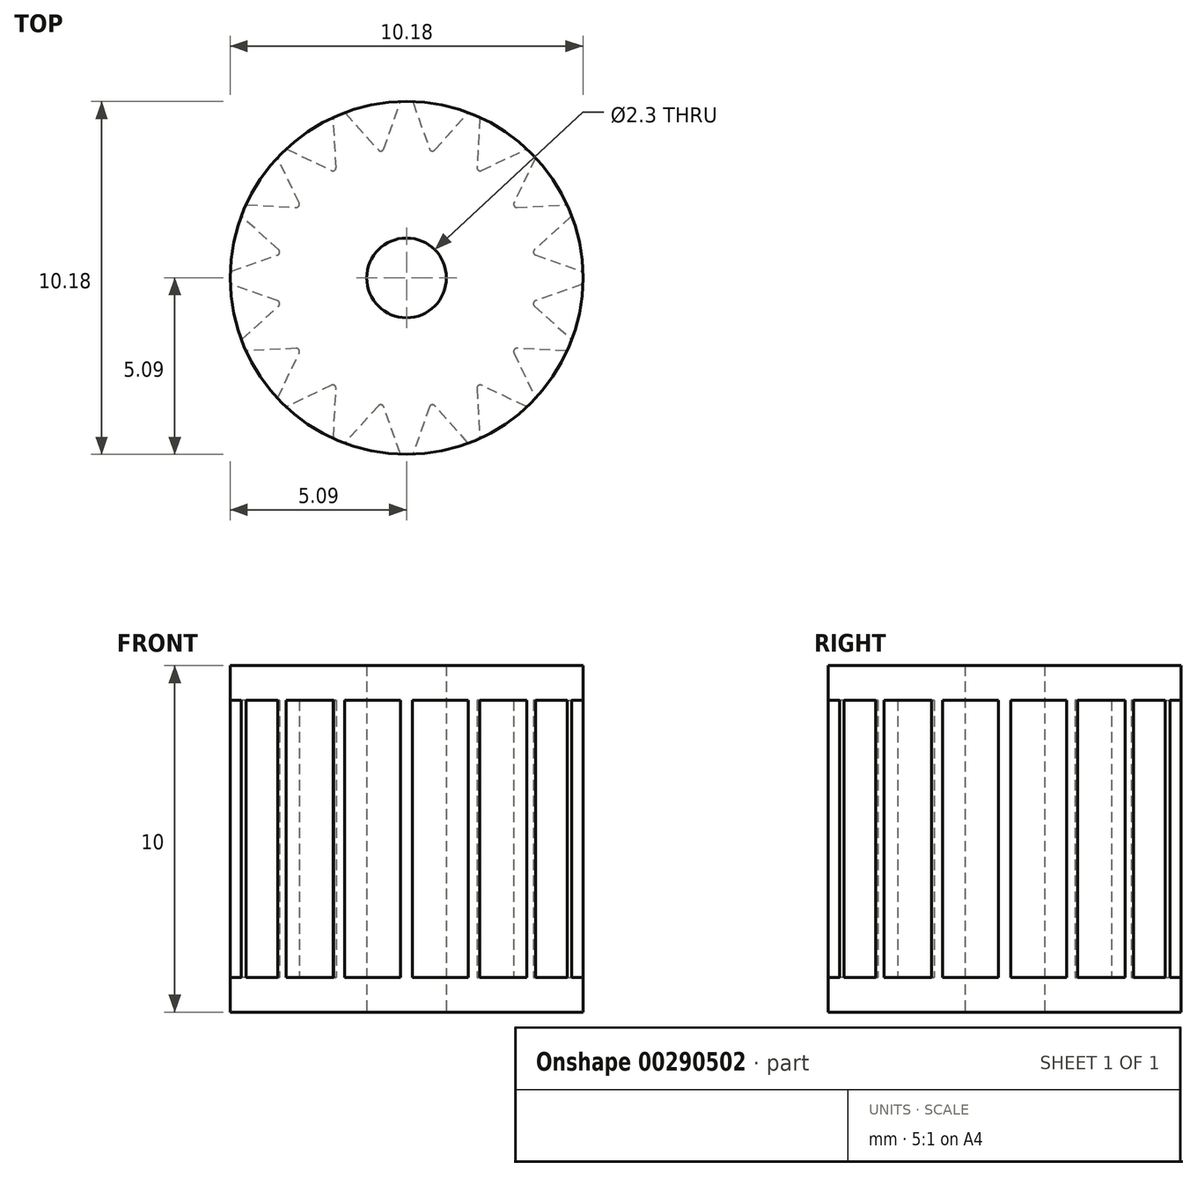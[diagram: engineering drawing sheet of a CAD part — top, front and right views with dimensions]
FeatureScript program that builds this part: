
annotation { "Feature Type Name" : "Feature", "Feature Type Description" : "" }
export const myFeature = defineFeature(function(context is Context, id is Id, definition is map)
    precondition{}
    {
        {
            var Q0;
            Q0=qCreatedBy(makeId("Top.planeOp"),FACE);
            var sketch = newSketch(context, id + "F0", { "sketchPlane" : qUnion([Q0])});
            skCircle(sketch, "E0", {"center": v(0, 0) * mm, "radius": 1.15 * mm});
            skCircle(sketch, "E1", {"center": v(0, 0) * mm, "radius": 5.1 * mm});
            skLineSegment(sketch, "E2", {"start": v(0, 5.1) * mm, "end": v(0, 0) * mm});
            skLineSegment(sketch, "E3.1.0", {"start": v(-1.95, 4.7) * mm, "end": v(0, 0) * mm});
            skLineSegment(sketch, "E3.2.0", {"start": v(-3.6, 3.6) * mm, "end": v(0, 0) * mm});
            skLineSegment(sketch, "E3.3.0", {"start": v(-4.7, 1.95) * mm, "end": v(0, 0) * mm});
            skLineSegment(sketch, "E3.4.0", {"start": v(-5.1, 0) * mm, "end": v(0, 0) * mm});
            skLineSegment(sketch, "E3.5.0", {"start": v(-4.7, -1.95) * mm, "end": v(0, 0) * mm});
            skLineSegment(sketch, "E3.6.0", {"start": v(-3.6, -3.6) * mm, "end": v(0, 0) * mm});
            skLineSegment(sketch, "E3.7.0", {"start": v(-1.95, -4.7) * mm, "end": v(0, 0) * mm});
            skLineSegment(sketch, "E3.8.0", {"start": v(0, -5.1) * mm, "end": v(0, 0) * mm});
            skLineSegment(sketch, "E3.9.0", {"start": v(1.95, -4.7) * mm, "end": v(0, 0) * mm});
            skLineSegment(sketch, "E3.10.0", {"start": v(3.6, -3.6) * mm, "end": v(0, 0) * mm});
            skLineSegment(sketch, "E3.11.0", {"start": v(4.7, -1.95) * mm, "end": v(0, 0) * mm});
            skLineSegment(sketch, "E3.12.0", {"start": v(5.1, 0) * mm, "end": v(0, 0) * mm});
            skLineSegment(sketch, "E3.13.0", {"start": v(4.7, 1.95) * mm, "end": v(0, 0) * mm});
            skLineSegment(sketch, "E3.14.0", {"start": v(3.6, 3.6) * mm, "end": v(0, 0) * mm});
            skLineSegment(sketch, "E3.15.0", {"start": v(1.95, 4.7) * mm, "end": v(0, 0) * mm});
            skCircle(sketch, "E4.0", {"center": v(0, 0) * mm, "radius": 5.6 * mm});
            skLineSegment(sketch, "E5", {"start": v(0, 5.1) * mm, "end": v(0, 5.2) * mm});
            skLineSegment(sketch, "E6.1.0", {"start": v(-1.95, 4.7) * mm, "end": v(-2.14, 5.17) * mm});
            skLineSegment(sketch, "E6.2.0", {"start": v(-3.6, 3.6) * mm, "end": v(-3.95, 3.95) * mm});
            skLineSegment(sketch, "E6.3.0", {"start": v(-4.7, 1.95) * mm, "end": v(-5.17, 2.14) * mm});
            skLineSegment(sketch, "E6.4.0", {"start": v(-5.1, 0) * mm, "end": v(-5.6, 0) * mm});
            skLineSegment(sketch, "E6.5.0", {"start": v(-4.7, -1.95) * mm, "end": v(-5.17, -2.14) * mm});
            skLineSegment(sketch, "E6.6.0", {"start": v(-3.6, -3.6) * mm, "end": v(-3.95, -3.95) * mm});
            skLineSegment(sketch, "E6.7.0", {"start": v(-1.95, -4.7) * mm, "end": v(-2.14, -5.17) * mm});
            skLineSegment(sketch, "E6.8.0", {"start": v(0, -5.1) * mm, "end": v(0, -5.6) * mm});
            skLineSegment(sketch, "E6.9.0", {"start": v(1.95, -4.7) * mm, "end": v(2.14, -5.17) * mm});
            skLineSegment(sketch, "E6.10.0", {"start": v(3.6, -3.6) * mm, "end": v(3.95, -3.95) * mm});
            skLineSegment(sketch, "E6.11.0", {"start": v(4.7, -1.95) * mm, "end": v(5.17, -2.14) * mm});
            skLineSegment(sketch, "E6.12.0", {"start": v(5.1, 0) * mm, "end": v(5.6, 0) * mm});
            skLineSegment(sketch, "E6.13.0", {"start": v(4.7, 1.95) * mm, "end": v(5.17, 2.14) * mm});
            skLineSegment(sketch, "E6.14.0", {"start": v(3.6, 3.6) * mm, "end": v(3.95, 3.95) * mm});
            skLineSegment(sketch, "E6.15.0", {"start": v(1.95, 4.7) * mm, "end": v(2.14, 5.17) * mm});
            skLineSegment(sketch, "E7", {"start": v(0.19, 5.06) * mm, "end": v(0.19, 5.06) * mm});
            skLineSegment(sketch, "E8", {"start": v(0.82, 3.7) * mm, "end": v(1.76, 4.75) * mm});
            skPoint(sketch, "E9.visualSharp", {"position": v(0.71, 3.58) * mm});
            skArc(sketch, "E9.filletArc", {"start": v(0.66, 3.72) * mm, "mid": v(0.73, 3.66) * mm, "end": v(0.82, 3.7) * mm});
            skLineSegment(sketch, "E10.MirrorCS", {"start": v(-0.19, 5.06) * mm, "end": v(-0.66, 3.72) * mm});
            skLineSegment(sketch, "E11.MirrorCS", {"start": v(2.03, 3.19) * mm, "end": v(2.11, 4.6) * mm});
            skPoint(sketch, "E12.visualSharp", {"position": v(0, 5.6) * mm});
            skArc(sketch, "E12.filletArc", {"start": v(0.19, 5.06) * mm, "mid": v(0.12, 5.16) * mm, "end": v(0, 5.2) * mm});
            skPoint(sketch, "E13.visualSharp", {"position": v(2.14, 5.17) * mm});
            skArc(sketch, "E13.filletArc", {"start": v(2.11, 4.6) * mm, "mid": v(2.08, 4.72) * mm, "end": v(1.99, 4.8) * mm});
            skLineSegment(sketch, "E14", {"start": v(0, 5.2) * mm, "end": v(0, 5.6) * mm});
            skLineSegment(sketch, "E15", {"start": v(1.99, 4.8) * mm, "end": v(1.99, 4.8) * mm});
            skLineSegment(sketch, "E16", {"start": v(0.19, 5.06) * mm, "end": v(0.66, 3.72) * mm});
            skArc(sketch, "E17", {"start": v(0, 5.2) * mm, "mid": v(-0.12, 5.16) * mm, "end": v(-0.19, 5.06) * mm});
            skLineSegment(sketch, "E18", {"start": v(1.76, 4.75) * mm, "end": v(1.76, 4.75) * mm});
            skArc(sketch, "E19", {"start": v(1.99, 4.8) * mm, "mid": v(1.87, 4.8) * mm, "end": v(1.76, 4.75) * mm});
            skSolve(sketch);
        }
        {
            var Q0;
            {var subQ11=sQuery(id+"F0.wireOp",EDGE,"E8");Q0=makeQuery(id+"F0.imprint","IMPRINT",FACE,{"disambiguationData":[TD([[makeQuery(id+"F0.imprint","IMPRINT",EDGE,{"derivedFrom":subQ11}),-1.0]])]});}
            var Q1;
            {var subQ0=sQuery(id+"F0.wireOp",EDGE,"E3.15.0");var subQ1=sQuery(id+"F0.wireOp",EDGE,"E0");var subQ2=makeQuery(id+"F0.imprint","INTERSECT",VERTEX,{"derivedFrom":[subQ1,subQ0]});Q1=makeQuery(id+"F0.imprint","IMPRINT",FACE,{"disambiguationData":[TD([[makeQuery(id+"F0.imprint","IMPRINT",EDGE,{"disambiguationData":[TD([[subQ2,-1.0]])],"derivedFrom":subQ1}),1.0]])]});}
            extrude(context, id + "F1", {"entities" : qUnion([Q0, Q1]), "depth" : 8 * mm});
        }
        {
            var Q0;
            Q0=makeQuery(id+"F1.opExtrude","SWEPT_BODY",BODY,{"disambiguationData":[OSD([sQuery(id+"F0.wireOp",EDGE,"E1"),sQuery(id+"F0.wireOp",EDGE,"E2"),sQuery(id+"F0.wireOp",EDGE,"E3.15.0"),sQuery(id+"F0.wireOp",EDGE,"E8"),sQuery(id+"F0.wireOp",EDGE,"E9.filletArc"),sQuery(id+"F0.wireOp",EDGE,"E12.filletArc"),sQuery(id+"F0.wireOp",EDGE,"E16"),sQuery(id+"F0.wireOp",EDGE,"E19")])]});
            var Q1;
            Q1=sQuery(id+"F0.wireOp",EDGE,"E1");
            circularPattern(context, id + "F2", {"operationType" : NewBodyOperationType.ADD, "entities" : qUnion([Q0]), "axis" : qUnion([Q1]), "angle" : 360 * degree, "instanceCount" : 16, "equalSpace" : true});
        }
        {
            var Q0;
            {var subQ0=sQuery(id+"F0.wireOp",EDGE,"E3.1.0");var subQ1=sQuery(id+"F0.wireOp",EDGE,"E0");var subQ2=makeQuery(id+"F0.imprint","INTERSECT",VERTEX,{"derivedFrom":[subQ1,subQ0]});Q0=makeQuery(id+"F0.imprint","IMPRINT",FACE,{"disambiguationData":[TD([[makeQuery(id+"F0.imprint","IMPRINT",EDGE,{"disambiguationData":[TD([[subQ2,-1.0]])],"derivedFrom":subQ1}),1.0]])]});}
            var Q1;
            {var subQ0=sQuery(id+"F0.wireOp",EDGE,"E2");var subQ1=sQuery(id+"F0.wireOp",EDGE,"E0");var subQ2=makeQuery(id+"F0.imprint","INTERSECT",VERTEX,{"derivedFrom":[subQ1,subQ0]});Q1=makeQuery(id+"F0.imprint","IMPRINT",FACE,{"disambiguationData":[TD([[makeQuery(id+"F0.imprint","IMPRINT",EDGE,{"disambiguationData":[TD([[subQ2,-1.0]])],"derivedFrom":subQ1}),1.0]])]});}
            var Q2;
            {var subQ0=sQuery(id+"F0.wireOp",EDGE,"E3.15.0");var subQ1=sQuery(id+"F0.wireOp",EDGE,"E0");var subQ2=makeQuery(id+"F0.imprint","INTERSECT",VERTEX,{"derivedFrom":[subQ1,subQ0]});Q2=makeQuery(id+"F0.imprint","IMPRINT",FACE,{"disambiguationData":[TD([[makeQuery(id+"F0.imprint","IMPRINT",EDGE,{"disambiguationData":[TD([[subQ2,-1.0]])],"derivedFrom":subQ1}),1.0]])]});}
            var Q3;
            {var subQ0=sQuery(id+"F0.wireOp",EDGE,"E3.14.0");var subQ1=sQuery(id+"F0.wireOp",EDGE,"E0");var subQ2=makeQuery(id+"F0.imprint","INTERSECT",VERTEX,{"derivedFrom":[subQ1,subQ0]});Q3=makeQuery(id+"F0.imprint","IMPRINT",FACE,{"disambiguationData":[TD([[makeQuery(id+"F0.imprint","IMPRINT",EDGE,{"disambiguationData":[TD([[subQ2,-1.0]])],"derivedFrom":subQ1}),1.0]])]});}
            var Q4;
            {var subQ0=sQuery(id+"F0.wireOp",EDGE,"E3.2.0");var subQ1=sQuery(id+"F0.wireOp",EDGE,"E0");var subQ2=makeQuery(id+"F0.imprint","INTERSECT",VERTEX,{"derivedFrom":[subQ1,subQ0]});Q4=makeQuery(id+"F0.imprint","IMPRINT",FACE,{"disambiguationData":[TD([[makeQuery(id+"F0.imprint","IMPRINT",EDGE,{"disambiguationData":[TD([[subQ2,-1.0]])],"derivedFrom":subQ1}),1.0]])]});}
            var Q5;
            {var subQ0=sQuery(id+"F0.wireOp",EDGE,"E3.3.0");var subQ1=sQuery(id+"F0.wireOp",EDGE,"E0");var subQ2=makeQuery(id+"F0.imprint","INTERSECT",VERTEX,{"derivedFrom":[subQ1,subQ0]});Q5=makeQuery(id+"F0.imprint","IMPRINT",FACE,{"disambiguationData":[TD([[makeQuery(id+"F0.imprint","IMPRINT",EDGE,{"disambiguationData":[TD([[subQ2,-1.0]])],"derivedFrom":subQ1}),1.0]])]});}
            var Q6;
            {var subQ0=sQuery(id+"F0.wireOp",EDGE,"E3.4.0");var subQ1=sQuery(id+"F0.wireOp",EDGE,"E0");var subQ2=makeQuery(id+"F0.imprint","INTERSECT",VERTEX,{"derivedFrom":[subQ1,subQ0]});Q6=makeQuery(id+"F0.imprint","IMPRINT",FACE,{"disambiguationData":[TD([[makeQuery(id+"F0.imprint","IMPRINT",EDGE,{"disambiguationData":[TD([[subQ2,-1.0]])],"derivedFrom":subQ1}),1.0]])]});}
            var Q7;
            {var subQ0=sQuery(id+"F0.wireOp",EDGE,"E3.5.0");var subQ1=sQuery(id+"F0.wireOp",EDGE,"E0");var subQ2=makeQuery(id+"F0.imprint","INTERSECT",VERTEX,{"derivedFrom":[subQ1,subQ0]});Q7=makeQuery(id+"F0.imprint","IMPRINT",FACE,{"disambiguationData":[TD([[makeQuery(id+"F0.imprint","IMPRINT",EDGE,{"disambiguationData":[TD([[subQ2,-1.0]])],"derivedFrom":subQ1}),1.0]])]});}
            var Q8;
            {var subQ0=sQuery(id+"F0.wireOp",EDGE,"E3.6.0");var subQ1=sQuery(id+"F0.wireOp",EDGE,"E0");var subQ2=makeQuery(id+"F0.imprint","INTERSECT",VERTEX,{"derivedFrom":[subQ1,subQ0]});Q8=makeQuery(id+"F0.imprint","IMPRINT",FACE,{"disambiguationData":[TD([[makeQuery(id+"F0.imprint","IMPRINT",EDGE,{"disambiguationData":[TD([[subQ2,-1.0]])],"derivedFrom":subQ1}),1.0]])]});}
            var Q9;
            {var subQ0=sQuery(id+"F0.wireOp",EDGE,"E3.7.0");var subQ1=sQuery(id+"F0.wireOp",EDGE,"E0");var subQ2=makeQuery(id+"F0.imprint","INTERSECT",VERTEX,{"derivedFrom":[subQ1,subQ0]});Q9=makeQuery(id+"F0.imprint","IMPRINT",FACE,{"disambiguationData":[TD([[makeQuery(id+"F0.imprint","IMPRINT",EDGE,{"disambiguationData":[TD([[subQ2,-1.0]])],"derivedFrom":subQ1}),1.0]])]});}
            var Q10;
            {var subQ0=sQuery(id+"F0.wireOp",EDGE,"E3.8.0");var subQ1=sQuery(id+"F0.wireOp",EDGE,"E0");var subQ2=makeQuery(id+"F0.imprint","INTERSECT",VERTEX,{"derivedFrom":[subQ1,subQ0]});Q10=makeQuery(id+"F0.imprint","IMPRINT",FACE,{"disambiguationData":[TD([[makeQuery(id+"F0.imprint","IMPRINT",EDGE,{"disambiguationData":[TD([[subQ2,-1.0]])],"derivedFrom":subQ1}),1.0]])]});}
            var Q11;
            {var subQ0=sQuery(id+"F0.wireOp",EDGE,"E3.9.0");var subQ1=sQuery(id+"F0.wireOp",EDGE,"E0");var subQ2=makeQuery(id+"F0.imprint","INTERSECT",VERTEX,{"derivedFrom":[subQ1,subQ0]});Q11=makeQuery(id+"F0.imprint","IMPRINT",FACE,{"disambiguationData":[TD([[makeQuery(id+"F0.imprint","IMPRINT",EDGE,{"disambiguationData":[TD([[subQ2,-1.0]])],"derivedFrom":subQ1}),1.0]])]});}
            var Q12;
            {var subQ0=sQuery(id+"F0.wireOp",EDGE,"E3.10.0");var subQ1=sQuery(id+"F0.wireOp",EDGE,"E0");var subQ2=makeQuery(id+"F0.imprint","INTERSECT",VERTEX,{"derivedFrom":[subQ1,subQ0]});Q12=makeQuery(id+"F0.imprint","IMPRINT",FACE,{"disambiguationData":[TD([[makeQuery(id+"F0.imprint","IMPRINT",EDGE,{"disambiguationData":[TD([[subQ2,-1.0]])],"derivedFrom":subQ1}),1.0]])]});}
            var Q13;
            {var subQ0=sQuery(id+"F0.wireOp",EDGE,"E3.12.0");var subQ1=sQuery(id+"F0.wireOp",EDGE,"E0");var subQ2=makeQuery(id+"F0.imprint","INTERSECT",VERTEX,{"derivedFrom":[subQ1,subQ0]});Q13=makeQuery(id+"F0.imprint","IMPRINT",FACE,{"disambiguationData":[TD([[makeQuery(id+"F0.imprint","IMPRINT",EDGE,{"disambiguationData":[TD([[subQ2,1.0]])],"derivedFrom":subQ1}),1.0]])]});}
            var Q14;
            {var subQ0=sQuery(id+"F0.wireOp",EDGE,"E3.13.0");var subQ1=sQuery(id+"F0.wireOp",EDGE,"E0");var subQ2=makeQuery(id+"F0.imprint","INTERSECT",VERTEX,{"derivedFrom":[subQ1,subQ0]});Q14=makeQuery(id+"F0.imprint","IMPRINT",FACE,{"disambiguationData":[TD([[makeQuery(id+"F0.imprint","IMPRINT",EDGE,{"disambiguationData":[TD([[subQ2,1.0]])],"derivedFrom":subQ1}),1.0]])]});}
            var Q15;
            {var subQ0=sQuery(id+"F0.wireOp",EDGE,"E3.13.0");var subQ1=sQuery(id+"F0.wireOp",EDGE,"E0");var subQ2=makeQuery(id+"F0.imprint","INTERSECT",VERTEX,{"derivedFrom":[subQ1,subQ0]});Q15=makeQuery(id+"F0.imprint","IMPRINT",FACE,{"disambiguationData":[TD([[makeQuery(id+"F0.imprint","IMPRINT",EDGE,{"disambiguationData":[TD([[subQ2,-1.0]])],"derivedFrom":subQ1}),1.0]])]});}
            extrude(context, id + "F3", {"entities" : qUnion([Q0, Q1, Q2, Q3, Q4, Q5, Q6, Q7, Q8, Q9, Q10, Q11, Q12, Q13, Q14, Q15]), "operationType" : NewBodyOperationType.REMOVE, "depth" : 25 * mm});
        }
        {
            var Q0;
            {var subQ0=sQuery(id+"F0.wireOp",EDGE,"E3.1.0");var subQ1=sQuery(id+"F0.wireOp",EDGE,"E0");var subQ2=makeQuery(id+"F0.imprint","INTERSECT",VERTEX,{"derivedFrom":[subQ1,subQ0]});Q0=makeQuery(id+"F0.imprint","IMPRINT",FACE,{"disambiguationData":[TD([[makeQuery(id+"F0.imprint","IMPRINT",EDGE,{"disambiguationData":[TD([[subQ2,-1.0]])],"derivedFrom":subQ1}),-1.0]])]});}
            var sketch = newSketch(context, id + "F4", { "sketchPlane" : qUnion([Q0])});
            skCircle(sketch, "E20.0", {"center": v(0, 0) * mm, "radius": 5.1 * mm});
            skCircle(sketch, "E20.1", {"center": v(0, 0) * mm, "radius": 1.15 * mm});
            skSolve(sketch);
        }
        {
            var Q0;
            Q0 = qSketchRegion(id + "F4", true);
            extrude(context, id + "F5", {"entities" : qUnion([Q0]), "operationType" : NewBodyOperationType.ADD, "oppositeDirection" : true, "depth" : 1 * mm});
        }
        {
            var Q0;
            {var subQ0=makeQuery(id+"F1.opExtrude","CAP_FACE",FACE,{"disambiguationData":[OSD([sQuery(id+"F0.wireOp",EDGE,"E1"),sQuery(id+"F0.wireOp",EDGE,"E2"),sQuery(id+"F0.wireOp",EDGE,"E3.15.0"),sQuery(id+"F0.wireOp",EDGE,"E8"),sQuery(id+"F0.wireOp",EDGE,"E9.filletArc"),sQuery(id+"F0.wireOp",EDGE,"E12.filletArc"),sQuery(id+"F0.wireOp",EDGE,"E16"),sQuery(id+"F0.wireOp",EDGE,"E19")])],"isStart":false});Q0=makeQuery(id+"F2.boolean.opBoolean","MERGE",FACE,{"derivedFrom":[subQ0,makeQuery(id+"F2.opPattern","COPY",FACE,{"derivedFrom":subQ0,"instanceName":"1"}),makeQuery(id+"F2.opPattern","COPY",FACE,{"derivedFrom":subQ0,"instanceName":"2"}),makeQuery(id+"F2.opPattern","COPY",FACE,{"derivedFrom":subQ0,"instanceName":"3"}),makeQuery(id+"F2.opPattern","COPY",FACE,{"derivedFrom":subQ0,"instanceName":"4"}),makeQuery(id+"F2.opPattern","COPY",FACE,{"derivedFrom":subQ0,"instanceName":"5"}),makeQuery(id+"F2.opPattern","COPY",FACE,{"derivedFrom":subQ0,"instanceName":"6"}),makeQuery(id+"F2.opPattern","COPY",FACE,{"derivedFrom":subQ0,"instanceName":"7"}),makeQuery(id+"F2.opPattern","COPY",FACE,{"derivedFrom":subQ0,"instanceName":"8"}),makeQuery(id+"F2.opPattern","COPY",FACE,{"derivedFrom":subQ0,"instanceName":"9"}),makeQuery(id+"F2.opPattern","COPY",FACE,{"derivedFrom":subQ0,"instanceName":"10"}),makeQuery(id+"F2.opPattern","COPY",FACE,{"derivedFrom":subQ0,"instanceName":"11"}),makeQuery(id+"F2.opPattern","COPY",FACE,{"derivedFrom":subQ0,"instanceName":"12"}),makeQuery(id+"F2.opPattern","COPY",FACE,{"derivedFrom":subQ0,"instanceName":"13"}),makeQuery(id+"F2.opPattern","COPY",FACE,{"derivedFrom":subQ0,"instanceName":"14"}),makeQuery(id+"F2.opPattern","COPY",FACE,{"derivedFrom":subQ0,"instanceName":"15"})]});}
            var sketch = newSketch(context, id + "F6", { "sketchPlane" : qUnion([Q0])});
            skCircle(sketch, "E21.0", {"center": v(0, 0) * mm, "radius": 1.15 * mm});
            skCircle(sketch, "E21.1", {"center": v(0, 0) * mm, "radius": 5.1 * mm});
            skSolve(sketch);
        }
        {
            var Q0;
            Q0 = qSketchRegion(id + "F6", true);
            extrude(context, id + "F7", {"entities" : qUnion([Q0]), "operationType" : NewBodyOperationType.ADD, "depth" : 1 * mm});
        }
    });
